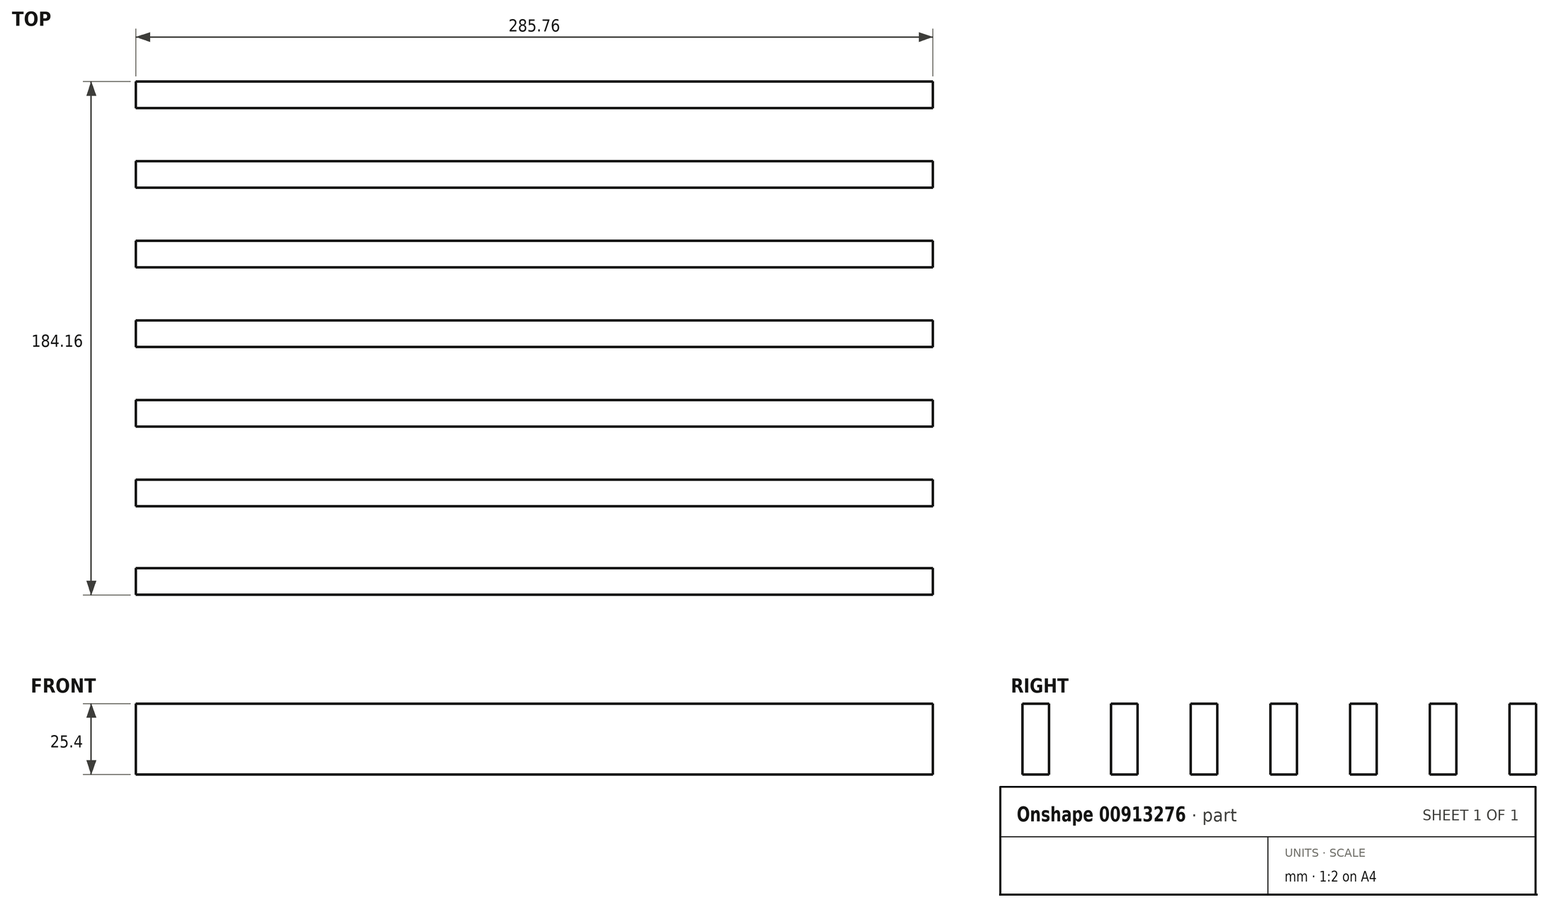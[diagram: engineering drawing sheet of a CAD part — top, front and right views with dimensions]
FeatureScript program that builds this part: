
annotation { "Feature Type Name" : "Feature", "Feature Type Description" : "" }
export const myFeature = defineFeature(function(context is Context, id is Id, definition is map)
    precondition{}
    {
        {
            var Q0;
            Q0=qCreatedBy(makeId("Top.planeOp"),FACE);
            var sketch = newSketch(context, id + "F0", { "sketchPlane" : qUnion([Q0])});
            skLineSegment(sketch, "E0.bottom", {"start": v(152.4, 92.08) * mm, "end": v(-152.4, 92.08) * mm});
            skLineSegment(sketch, "E0.top", {"start": v(152.4, -92.08) * mm, "end": v(-152.4, -92.08) * mm});
            skLineSegment(sketch, "E0.left", {"start": v(152.4, 92.08) * mm, "end": v(152.4, -92.08) * mm});
            skLineSegment(sketch, "E0.right", {"start": v(-152.4, 92.08) * mm, "end": v(-152.4, -92.08) * mm});
            skPoint(sketch, "E0.middle", {"position": v(0, 0) * mm});
            skLineSegment(sketch, "E1.0", {"start": v(142.87, 82.55) * mm, "end": v(-142.88, 82.55) * mm});
            skLineSegment(sketch, "E2.0", {"start": v(-142.88, 92.08) * mm, "end": v(-142.88, -92.08) * mm});
            skLineSegment(sketch, "E3.0", {"start": v(142.87, 92.08) * mm, "end": v(142.87, -92.08) * mm});
            skLineSegment(sketch, "E4.0", {"start": v(142.87, -82.55) * mm, "end": v(-142.88, -82.55) * mm});
            skLineSegment(sketch, "E5.bottom", {"start": v(-142.88, 63.5) * mm, "end": v(142.87, 63.5) * mm});
            skLineSegment(sketch, "E5.top", {"start": v(-142.88, 53.97) * mm, "end": v(142.87, 53.98) * mm});
            skLineSegment(sketch, "E5.left", {"start": v(-142.88, 63.5) * mm, "end": v(-142.88, 53.97) * mm});
            skLineSegment(sketch, "E5.right", {"start": v(142.87, 63.5) * mm, "end": v(142.87, 53.98) * mm});
            skLineSegment(sketch, "E6.bottom", {"start": v(-142.88, 34.93) * mm, "end": v(142.87, 34.93) * mm});
            skLineSegment(sketch, "E6.top", {"start": v(-142.88, 25.4) * mm, "end": v(142.87, 25.4) * mm});
            skLineSegment(sketch, "E6.left", {"start": v(-142.88, 34.93) * mm, "end": v(-142.88, 25.4) * mm});
            skLineSegment(sketch, "E6.right", {"start": v(142.87, 34.93) * mm, "end": v(142.87, 25.4) * mm});
            skLineSegment(sketch, "E7.bottom", {"start": v(-142.88, 6.35) * mm, "end": v(142.87, 6.35) * mm});
            skLineSegment(sketch, "E7.top", {"start": v(-142.88, -3.18) * mm, "end": v(142.87, -3.17) * mm});
            skLineSegment(sketch, "E7.left", {"start": v(-142.88, 6.35) * mm, "end": v(-142.88, -3.18) * mm});
            skLineSegment(sketch, "E7.right", {"start": v(142.87, 6.35) * mm, "end": v(142.87, -3.17) * mm});
            skLineSegment(sketch, "E8.bottom", {"start": v(-142.88, -22.23) * mm, "end": v(142.87, -22.22) * mm});
            skLineSegment(sketch, "E8.top", {"start": v(-142.88, -31.75) * mm, "end": v(142.87, -31.75) * mm});
            skLineSegment(sketch, "E8.left", {"start": v(-142.88, -22.23) * mm, "end": v(-142.88, -31.75) * mm});
            skLineSegment(sketch, "E8.right", {"start": v(142.87, -22.22) * mm, "end": v(142.87, -31.75) * mm});
            skLineSegment(sketch, "E9.bottom", {"start": v(-142.88, -50.8) * mm, "end": v(142.87, -50.8) * mm});
            skLineSegment(sketch, "E9.top", {"start": v(-142.88, -60.33) * mm, "end": v(142.87, -60.33) * mm});
            skLineSegment(sketch, "E9.left", {"start": v(-142.88, -50.8) * mm, "end": v(-142.88, -60.33) * mm});
            skLineSegment(sketch, "E9.right", {"start": v(142.87, -50.8) * mm, "end": v(142.87, -60.33) * mm});
            skSolve(sketch);
        }
        {
            var Q0;
            {var subQ5=sQuery(id+"F0.wireOp",EDGE,"E1.0");Q0=makeQuery(id+"F0.imprint","IMPRINT",FACE,{"disambiguationData":[TD([[makeQuery(id+"F0.imprint","IMPRINT",EDGE,{"derivedFrom":subQ5}),-1.0]])]});}
            var Q1;
            Q1=makeQuery(id+"F0.imprint","IMPRINT",FACE,{"disambiguationData":[TD([[makeQuery(id+"F0.imprint","IMPRINT",EDGE,{"derivedFrom":sQuery(id+"F0.wireOp",EDGE,"E5.bottom")}),-1.0]])]});
            var Q2;
            Q2=makeQuery(id+"F0.imprint","IMPRINT",FACE,{"disambiguationData":[TD([[makeQuery(id+"F0.imprint","IMPRINT",EDGE,{"derivedFrom":sQuery(id+"F0.wireOp",EDGE,"E6.bottom")}),-1.0]])]});
            var Q3;
            Q3=makeQuery(id+"F0.imprint","IMPRINT",FACE,{"disambiguationData":[TD([[makeQuery(id+"F0.imprint","IMPRINT",EDGE,{"derivedFrom":sQuery(id+"F0.wireOp",EDGE,"E7.bottom")}),-1.0]])]});
            var Q4;
            Q4=makeQuery(id+"F0.imprint","IMPRINT",FACE,{"disambiguationData":[TD([[makeQuery(id+"F0.imprint","IMPRINT",EDGE,{"derivedFrom":sQuery(id+"F0.wireOp",EDGE,"E8.bottom")}),-1.0]])]});
            var Q5;
            {var subQ5=sQuery(id+"F0.wireOp",EDGE,"E4.0");Q5=makeQuery(id+"F0.imprint","IMPRINT",FACE,{"disambiguationData":[TD([[makeQuery(id+"F0.imprint","IMPRINT",EDGE,{"derivedFrom":subQ5}),1.0]])]});}
            var Q6;
            Q6=makeQuery(id+"F0.imprint","IMPRINT",FACE,{"disambiguationData":[TD([[makeQuery(id+"F0.imprint","IMPRINT",EDGE,{"derivedFrom":sQuery(id+"F0.wireOp",EDGE,"E9.bottom")}),-1.0]])]});
            extrude(context, id + "F1", {"entities" : qUnion([Q0, Q1, Q2, Q3, Q4, Q5, Q6]), "depth" : 25.4 * mm, "offsetDistance" : 25.4 * mm});
        }
    });
